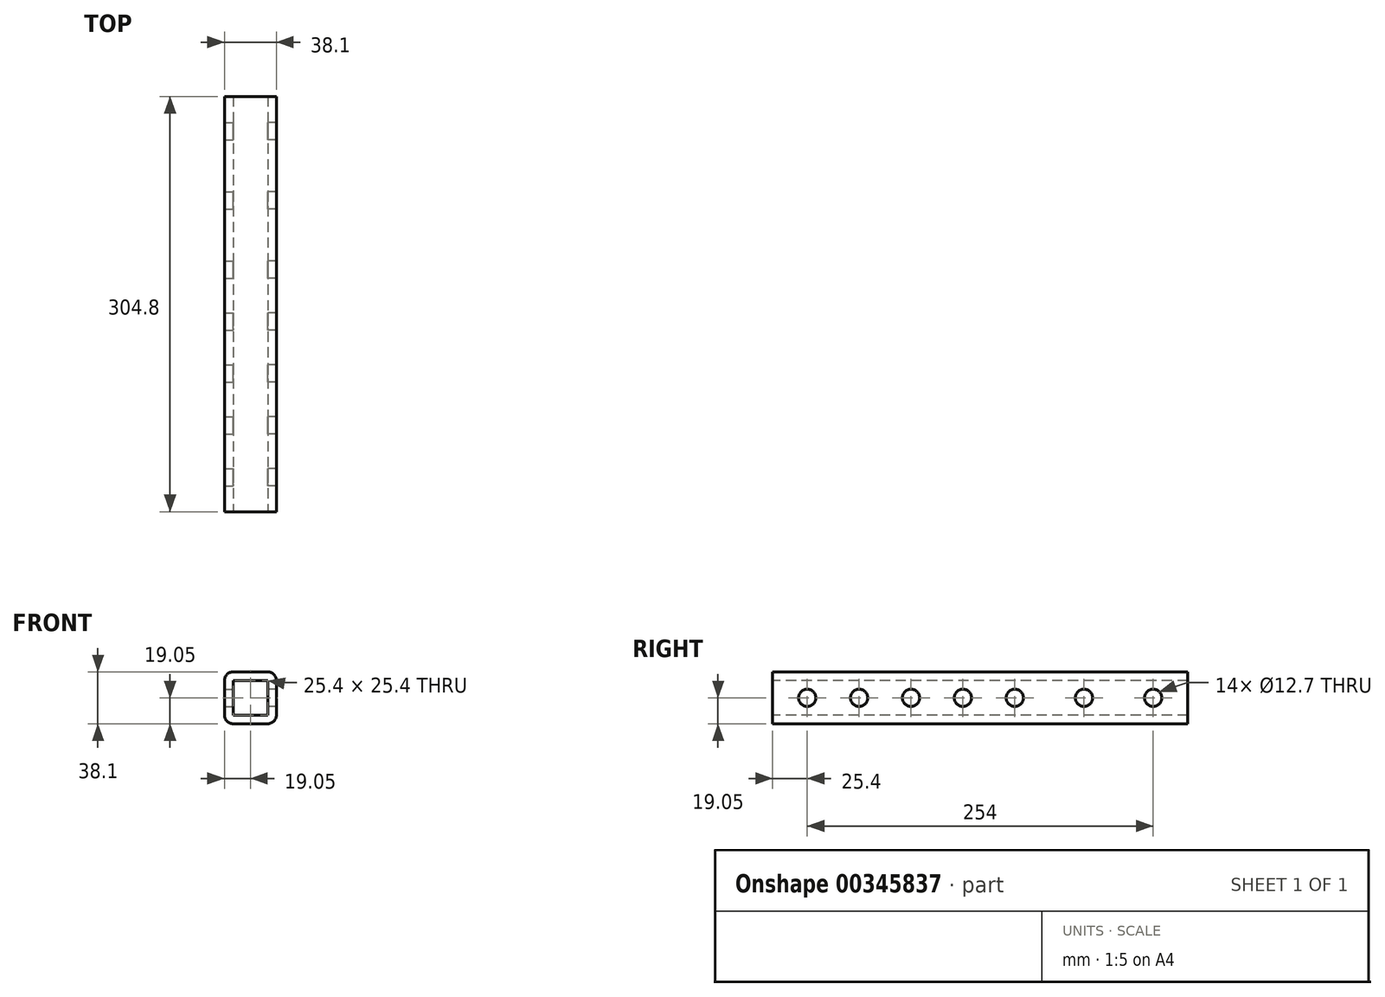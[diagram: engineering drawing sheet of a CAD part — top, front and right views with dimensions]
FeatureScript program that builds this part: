
annotation { "Feature Type Name" : "Feature", "Feature Type Description" : "" }
export const myFeature = defineFeature(function(context is Context, id is Id, definition is map)
    precondition{}
    {
        {
            var Q0;
            Q0=qCreatedBy(makeId("Front.planeOp"),FACE);
            var sketch = newSketch(context, id + "F0", { "sketchPlane" : qUnion([Q0])});
            skLineSegment(sketch, "E0.bottom", {"start": v(12.7, -19.05) * mm, "end": v(-12.7, -19.05) * mm});
            skLineSegment(sketch, "E0.top", {"start": v(12.7, 19.05) * mm, "end": v(-12.7, 19.05) * mm});
            skLineSegment(sketch, "E0.left", {"start": v(19.05, -12.7) * mm, "end": v(19.05, 12.7) * mm});
            skLineSegment(sketch, "E0.right", {"start": v(-19.05, -12.7) * mm, "end": v(-19.05, 12.7) * mm});
            skPoint(sketch, "E0.middle", {"position": v(0, 0) * mm});
            skPoint(sketch, "E1.visualSharp", {"position": v(-19.05, 19.05) * mm});
            skArc(sketch, "E1.filletArc", {"start": v(-12.7, 19.05) * mm, "mid": v(-17.2, 17.2) * mm, "end": v(-19.05, 12.7) * mm});
            skPoint(sketch, "E2.visualSharp", {"position": v(19.05, 19.05) * mm});
            skArc(sketch, "E2.filletArc", {"start": v(19.05, 12.7) * mm, "mid": v(17.2, 17.2) * mm, "end": v(12.7, 19.05) * mm});
            skPoint(sketch, "E3.visualSharp", {"position": v(19.05, -19.05) * mm});
            skArc(sketch, "E3.filletArc", {"start": v(12.7, -19.05) * mm, "mid": v(17.2, -17.2) * mm, "end": v(19.05, -12.7) * mm});
            skPoint(sketch, "E4.visualSharp", {"position": v(-19.05, -19.05) * mm});
            skArc(sketch, "E4.filletArc", {"start": v(-19.05, -12.7) * mm, "mid": v(-17.2, -17.2) * mm, "end": v(-12.7, -19.05) * mm});
            skPoint(sketch, "E5.left.end.orphan", {"position": v(6.35, 6.35) * mm});
            skPoint(sketch, "E5.right.start.orphan", {"position": v(-6.35, -6.35) * mm});
            skLineSegment(sketch, "E6.bottom", {"start": v(-12.7, -12.7) * mm, "end": v(12.7, -12.7) * mm});
            skLineSegment(sketch, "E6.top", {"start": v(-12.7, 12.7) * mm, "end": v(12.7, 12.7) * mm});
            skLineSegment(sketch, "E6.left", {"start": v(-12.7, -12.7) * mm, "end": v(-12.7, 12.7) * mm});
            skLineSegment(sketch, "E6.right", {"start": v(12.7, -12.7) * mm, "end": v(12.7, 12.7) * mm});
            skSolve(sketch);
        }
        {
            var Q0;
            Q0=makeQuery(id+"F0.imprint","IMPRINT",FACE,{"disambiguationData":[TD([[makeQuery(id+"F0.imprint","IMPRINT",EDGE,{"derivedFrom":sQuery(id+"F0.wireOp",EDGE,"E0.bottom")}),-1.0]])]});
            extrude(context, id + "F2", {"entities" : qUnion([Q0]), "oppositeDirection" : true, "depth" : 304.8 * mm});
        }
        {
            var Q0;
            Q0=qCreatedBy(makeId("Right.planeOp"),FACE);
            var sketch = newSketch(context, id + "F3", { "sketchPlane" : qUnion([Q0])});
            skPoint(sketch, "E7", {"position": v(50.8, 0) * mm});
            skPoint(sketch, "E8", {"position": v(25.4, 0) * mm});
            skPoint(sketch, "E9", {"position": v(63.5, 0) * mm});
            skPoint(sketch, "E10", {"position": v(101.6, 0) * mm});
            skPoint(sketch, "E11", {"position": v(139.7, 0) * mm});
            skPoint(sketch, "E12", {"position": v(431.8, 0) * mm});
            skPoint(sketch, "E13", {"position": v(381, 0) * mm});
            skPoint(sketch, "E14", {"position": v(228.6, 0) * mm});
            skPoint(sketch, "E15", {"position": v(279.4, 0) * mm});
            skPoint(sketch, "E16", {"position": v(177.8, 0) * mm});
            skSolve(sketch);
        }
        {
            var Q0;
            Q0=sQuery(id+"F3.wireOp",VERTEX,"E8");
            var Q1;
            Q1=sQuery(id+"F3.wireOp",VERTEX,"E10");
            var Q2;
            Q2=sQuery(id+"F3.wireOp",VERTEX,"E9");
            var Q3;
            Q3=sQuery(id+"F3.wireOp",VERTEX,"E14");
            var Q4;
            Q4=sQuery(id+"F3.wireOp",VERTEX,"E15");
            var Q5;
            Q5=sQuery(id+"F3.wireOp",VERTEX,"E11");
            var Q6;
            Q6=sQuery(id+"F3.wireOp",VERTEX,"E16");
            var Q7;
            Q7=makeQuery(id+"F2.opExtrude","SWEPT_BODY",BODY,{"disambiguationData":[OSD([sQuery(id+"F0.wireOp",EDGE,"E0.bottom"),sQuery(id+"F0.wireOp",EDGE,"E0.top"),sQuery(id+"F0.wireOp",EDGE,"E0.left"),sQuery(id+"F0.wireOp",EDGE,"E0.right"),sQuery(id+"F0.wireOp",EDGE,"E1.filletArc"),sQuery(id+"F0.wireOp",EDGE,"E2.filletArc"),sQuery(id+"F0.wireOp",EDGE,"E3.filletArc"),sQuery(id+"F0.wireOp",EDGE,"E4.filletArc"),sQuery(id+"F0.wireOp",EDGE,"E5.bottom"),sQuery(id+"F0.wireOp",EDGE,"E5.top"),sQuery(id+"F0.wireOp",EDGE,"E5.left"),sQuery(id+"F0.wireOp",EDGE,"E5.right")])]});
            hole(context, id + "F4", {"style" : HoleStyle.SIMPLE, "endStyle" : HoleEndStyle.THROUGH, "oppositeDirection" : true, "holeDiameter" : 12.7 * mm, "locations" : qUnion([Q0, Q1, Q2, Q3, Q4, Q5, Q6]), "scope" : qUnion([Q7]), "isTappedThrough" : true});
        }
        {
            var Q0;
            Q0=sQuery(id+"F3.wireOp",VERTEX,"E8");
            var Q1;
            Q1=sQuery(id+"F3.wireOp",VERTEX,"E9");
            var Q2;
            Q2=sQuery(id+"F3.wireOp",VERTEX,"E10");
            var Q3;
            Q3=sQuery(id+"F3.wireOp",VERTEX,"E14");
            var Q4;
            Q4=sQuery(id+"F3.wireOp",VERTEX,"E15");
            var Q5;
            Q5=sQuery(id+"F3.wireOp",VERTEX,"E11");
            var Q6;
            Q6=sQuery(id+"F3.wireOp",VERTEX,"E16");
            var Q7;
            Q7=makeQuery(id+"F2.opExtrude","SWEPT_BODY",BODY,{"disambiguationData":[OSD([sQuery(id+"F0.wireOp",EDGE,"E0.bottom"),sQuery(id+"F0.wireOp",EDGE,"E0.top"),sQuery(id+"F0.wireOp",EDGE,"E0.left"),sQuery(id+"F0.wireOp",EDGE,"E0.right"),sQuery(id+"F0.wireOp",EDGE,"E1.filletArc"),sQuery(id+"F0.wireOp",EDGE,"E2.filletArc"),sQuery(id+"F0.wireOp",EDGE,"E3.filletArc"),sQuery(id+"F0.wireOp",EDGE,"E4.filletArc"),sQuery(id+"F0.wireOp",EDGE,"E5.bottom"),sQuery(id+"F0.wireOp",EDGE,"E5.top"),sQuery(id+"F0.wireOp",EDGE,"E5.left"),sQuery(id+"F0.wireOp",EDGE,"E5.right")])]});
            hole(context, id + "F1", {"style" : HoleStyle.SIMPLE, "endStyle" : HoleEndStyle.THROUGH, "holeDiameter" : 12.7 * mm, "locations" : qUnion([Q0, Q1, Q2, Q3, Q4, Q5, Q6]), "scope" : qUnion([Q7]), "isTappedThrough" : true});
        }
    });
